# Revit family: Шкаф-корпус для ТГШн_КомплектацияLight_FedericaBugatti_R20
name_source: partatom
category: Оборудование
units: mm (PartAtom-declared; Revit-internal decimal feet)

## family parameters
Всегда вертикально = Да
Классификация = Нет
На основе рабочей плоскости = Нет
Общий = Нет
При загрузке вырезать с полостями = Нет
Размер круглого соединителя = Использовать диаметр
Тип детали = Нормальный
Точка расчета площади = Да

## types (2) — shared parameters
ADSK_Единица измерения = шт
ADSK_Завод-изготовитель = Federica Bugatti
ADSK_КПД = 92
ADSK_Классификация нагрузок = Прочее
ADSK_Количество = 1
ADSK_Количество фаз = 1
ADSK_Коэффициент мощности = 1
ADSK_Масса = 129
ADSK_Масса_Текст = 129
ADSK_Напряжение = 230 В
ADSK_Размер_Высота = 1252 мм
ADSK_Размер_Глубина = 606 мм
ADSK_Размер_Ширина = 806 мм
ADSK_Расход жидкости = 0.2 л/с
Материал_ВнешняяСтенка = ADSK_Металл_Окрашенный_Черный темный
Материал_Патрубки = ADSK_Металл_Сталь оцинкованная
zero-valued in all types: Отметка по умолчанию

## per-type parameters (varying)
| type | ADSK_Марка | ADSK_Наименование | ADSK_Номинальная мощность | ADSK_Полная мощность |
| BLOCK_24 | BLOCK 24 комплектация Light | Котел наружного размещения Federica Bugatti BLOCK 24 комплектация Light | 24300 Вт | 24300 В·А |
| BLOCK_32 | BLOCK 32 комплектация Light | Котел наружного размещения Federica Bugatti BLOCK 32 комплектация Light | 33300 Вт | 33300 В·А |
